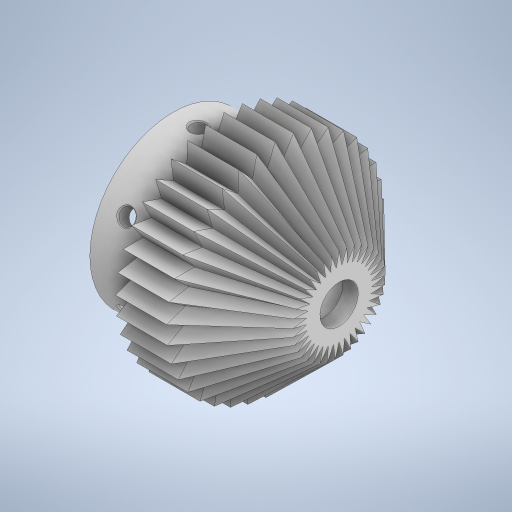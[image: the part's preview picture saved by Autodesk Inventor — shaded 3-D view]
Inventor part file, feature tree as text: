
AUTODESK INVENTOR PART (.ipt)
format: ipt  version: 2023 (Build 270158030, 158C)  size: 610,816 bytes
history: native  units: in
note: dims shown in document units (in); Inventor stores cm internally (conversion verified against a paired STEP export)
features: sketch x8, extrude x4, pattern_circular x3, other x2, loft x1, revolve x1, plane x1, hole x1
ambient origin geometry x8: Origin, YZ Plane, XZ Plane, XY Plane, X Axis, Y Axis, Z Axis, Center Point
bodies: Solid1 (feature_tree)
feature tree (21):
  other  "Main Body"
  extrude  "Teeth"  TaperAngle=45.0deg  [1 undecoded]
  pattern_circular  "Circular Pattern1"  Count=2  [1 undecoded]
  loft  "Angle Teeth"
  pattern_circular  "Circular Pattern2"  Count=37 Angle=360.0deg
  extrude  "Extrusion4"  Depth=0.3937in
  revolve  "Revolution2"  [1 undecoded]
  extrude  "Extrusion5"  Depth=0.3937in
  extrude  "Extrusion6"  Depth=0.3937in
  plane  "Work Plane1"
  hole  "Hole1"  [1 undecoded]
  pattern_circular  "Circular Pattern3"  Angle=90.0deg  [1 undecoded]
  sketch  "Sketch1"  dims[d0=0.7874in d1=45.0deg]
  sketch  "Sketch6"  dims[d2=0.5906in]
  sketch  "Sketch11"  dims[d3=2.5591in]
  other  "Edges2"
  sketch  "Sketch12"  dims[d4=90.0deg]
  sketch  "Sketch14"  dims[d18=45.0deg]
  sketch  "Sketch15"  dims[d19=0.3937in d20=0.7874in d21=0.0in]
  sketch  "Sketch16"  dims[d22=14.5669in d23=360.0deg d25=0.0in d26=90.0deg]
  sketch  "Sketch18"  dims[d27=0.0in d28=90.0deg d29=14.5669in d30=360.0deg d32=0.5906in d33=0.0in d34=0.0in d35=0.7874in d36=1.2205in d37=0.3937in d38=90.0deg d39=1.0236in d40=1.5354in d41=0.0in d42=0.7874in d43=0.0in d45=2.1654in d46=0.1969in d47=0.2362in d48=0.3389in d49=0.2756in d50=0.0787in d51=90.0deg d52=0.6167in d53=0.8108in d54=0.3937in d55=2.3622in d56=360.0deg]
note: 5 required parameter values undecoded (feature->parameter linkage not recoverable at this tier; creation-order binding heuristic only, values carry confidence <= 0.55)